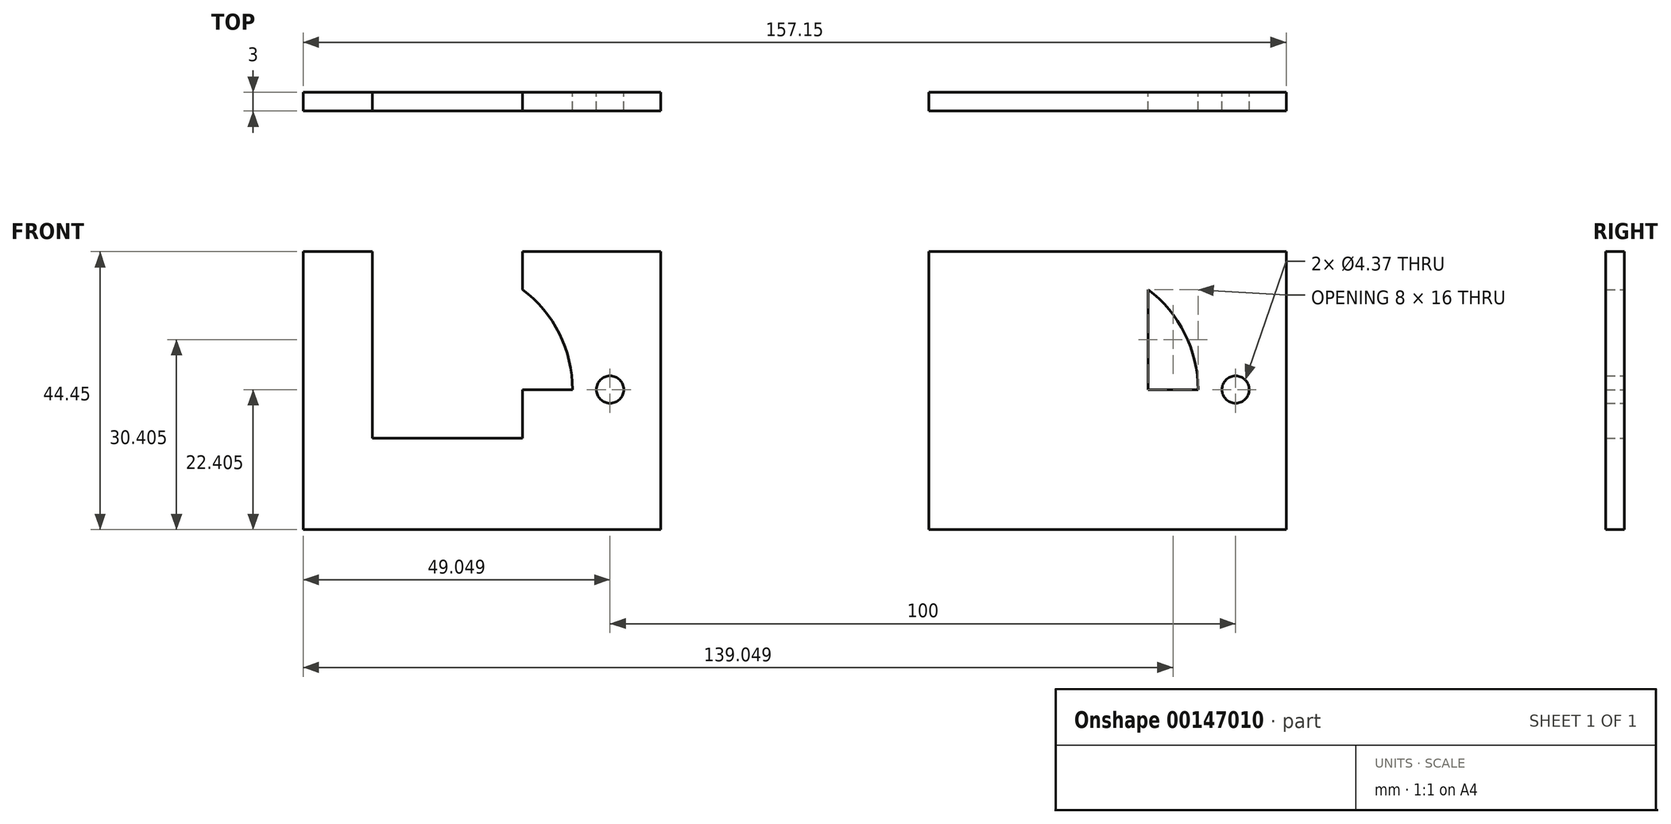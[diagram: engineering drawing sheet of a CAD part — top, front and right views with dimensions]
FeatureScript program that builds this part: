
annotation { "Feature Type Name" : "Feature", "Feature Type Description" : "" }
export const myFeature = defineFeature(function(context is Context, id is Id, definition is map)
    precondition{}
    {
        {
            var Q0;
            Q0=qCreatedBy(makeId("Front.planeOp"),FACE);
            var sketch = newSketch(context, id + "F0", { "sketchPlane" : qUnion([Q0])});
            skLineSegment(sketch, "E0.bottom", {"start": v(-38.32, 42.55) * mm, "end": v(34.07, 42.55) * mm});
            skLineSegment(sketch, "E0.top", {"start": v(-38.32, -29.84) * mm, "end": v(34.07, -29.84) * mm});
            skLineSegment(sketch, "E0.left", {"start": v(-38.32, 42.55) * mm, "end": v(-38.32, -29.84) * mm});
            skLineSegment(sketch, "E0.right", {"start": v(34.07, 42.55) * mm, "end": v(34.07, -29.84) * mm});
            skCircle(sketch, "E1", {"center": v(-10.8, -16.7) * mm, "radius": 2.18 * mm});
            skCircle(sketch, "E2", {"center": v(9.15, 5.72) * mm, "radius": 2.18 * mm});
            skCircle(sketch, "E3", {"center": v(9.15, 5.72) * mm, "radius": 20 * mm});
            skCircle(sketch, "E4", {"center": v(-10.8, -16.7) * mm, "radius": 10 * mm});
            skCircle(sketch, "E5", {"center": v(-13.28, 18.86) * mm, "radius": 20 * mm});
            skCircle(sketch, "E6", {"center": v(9.15, 5.72) * mm, "radius": 6 * mm});
            skCircle(sketch, "E7", {"center": v(-13.28, 18.86) * mm, "radius": 2.18 * mm});
            skLineSegment(sketch, "E8", {"start": v(-13.28, 18.86) * mm, "end": v(9.15, 5.72) * mm});
            skLineSegment(sketch, "E9", {"start": v(9.15, 5.72) * mm, "end": v(-10.8, -16.7) * mm});
            skLineSegment(sketch, "E10", {"start": v(-13.28, 18.86) * mm, "end": v(-13.28, 42.55) * mm});
            skLineSegment(sketch, "E11", {"start": v(-19.28, 42.55) * mm, "end": v(-19.28, 19.08) * mm});
            skLineSegment(sketch, "E12.MirrorCS", {"start": v(-7.28, 42.55) * mm, "end": v(-7.28, 19.08) * mm});
            skPoint(sketch, "E13.orphan", {"position": v(-7.28, 19.08) * mm});
            skLineSegment(sketch, "E14", {"start": v(-19.28, 19.08) * mm, "end": v(-19.28, 14.57) * mm});
            skLineSegment(sketch, "E15", {"start": v(-7.28, 19.08) * mm, "end": v(-7.28, 13.33) * mm});
            skLineSegment(sketch, "E16", {"start": v(-7.28, 13.33) * mm, "end": v(-19.28, 13.33) * mm});
            skLineSegment(sketch, "E17", {"start": v(-19.28, 13.33) * mm, "end": v(-19.28, 14.57) * mm});
            skLineSegment(sketch, "E18", {"start": v(-19.28, 42.55) * mm, "end": v(-19.28, 13.33) * mm});
            skLineSegment(sketch, "E19", {"start": v(-7.28, 42.55) * mm, "end": v(-7.28, 13.33) * mm});
            skLineSegment(sketch, "E20.bottom", {"start": v(-24.33, -118.82) * mm, "end": v(32.82, -118.82) * mm});
            skLineSegment(sketch, "E20.top", {"start": v(-24.33, -163.27) * mm, "end": v(32.82, -163.27) * mm});
            skLineSegment(sketch, "E20.left", {"start": v(-24.33, -118.82) * mm, "end": v(-24.33, -163.27) * mm});
            skLineSegment(sketch, "E20.right", {"start": v(32.82, -118.82) * mm, "end": v(32.82, -163.27) * mm});
            skCircle(sketch, "E21", {"center": v(24.72, -140.86) * mm, "radius": 2.18 * mm});
            skCircle(sketch, "E22", {"center": v(-1.28, -140.87) * mm, "radius": 20 * mm});
            skCircle(sketch, "E23", {"center": v(24.72, -140.86) * mm, "radius": 6 * mm});
            skCircle(sketch, "E24", {"center": v(-1.28, -140.87) * mm, "radius": 2.18 * mm});
            skLineSegment(sketch, "E25", {"start": v(-1.28, -140.87) * mm, "end": v(-1.28, -118.82) * mm});
            skLineSegment(sketch, "E26", {"start": v(-13.28, -118.82) * mm, "end": v(-13.28, -148.6) * mm});
            skLineSegment(sketch, "E27.MirrorCS", {"start": v(10.72, -118.82) * mm, "end": v(10.72, -148.6) * mm});
            skPoint(sketch, "E28.orphan", {"position": v(-1.28, -168.58) * mm});
            skLineSegment(sketch, "E29", {"start": v(10.72, -148.6) * mm, "end": v(-13.28, -148.6) * mm});
            skLineSegment(sketch, "E30", {"start": v(24.72, -140.86) * mm, "end": v(-1.28, -140.87) * mm});
            skSolve(sketch);
        }
        {
            var Q0;
            Q0=makeQuery(id+"F0.imprint","IMPRINT",FACE,{"disambiguationData":[TD([[makeQuery(id+"F0.imprint","IMPRINT",EDGE,{"derivedFrom":sQuery(id+"F0.wireOp",EDGE,"E20.top")}),1.0]])]});
            var Q1;
            {var subQ1=sQuery(id+"F0.wireOp",EDGE,"E29");Q1=makeQuery(id+"F0.imprint","IMPRINT",FACE,{"disambiguationData":[TD([[makeQuery(id+"F0.imprint","IMPRINT",EDGE,{"derivedFrom":subQ1}),1.0]])]});}
            var Q2;
            {var subQ0=sQuery(id+"F0.wireOp",EDGE,"E27.MirrorCS");var subQ1=sQuery(id+"F0.wireOp",EDGE,"E22");var subQ2=makeQuery(id+"F0.imprint","INTERSECT",VERTEX,{"derivedFrom":[subQ1,subQ0]});Q2=makeQuery(id+"F0.imprint","IMPRINT",FACE,{"disambiguationData":[TD([[makeQuery(id+"F0.imprint","IMPRINT",EDGE,{"disambiguationData":[TD([[subQ2,-1.0]])],"derivedFrom":subQ0}),1.0]])]});}
            var Q3;
            Q3=makeQuery(id+"F0.imprint","IMPRINT",FACE,{"disambiguationData":[TD([[makeQuery(id+"F0.imprint","IMPRINT",EDGE,{"derivedFrom":sQuery(id+"F0.wireOp",EDGE,"E21")}),-1.0]])]});
            extrude(context, id + "F1", {"entities" : qUnion([Q0, Q1, Q2, Q3]), "depth" : 3 * mm});
        }
        {
            var Q0;
            Q0=makeQuery(id+"F1.opExtrude","SWEPT_BODY",BODY,{"disambiguationData":[OSD([sQuery(id+"F0.wireOp",EDGE,"E20.bottom"),sQuery(id+"F0.wireOp",EDGE,"E20.top"),sQuery(id+"F0.wireOp",EDGE,"E20.left"),sQuery(id+"F0.wireOp",EDGE,"E20.right"),sQuery(id+"F0.wireOp",EDGE,"E21"),sQuery(id+"F0.wireOp",EDGE,"E29"),sQuery(id+"F0.wireOp",EDGE,"E26"),sQuery(id+"F0.wireOp",EDGE,"E27.MirrorCS")])]});
            transform(context, id + "F2", {"entities" : qUnion([Q0]), "transformType" : TransformType.TRANSLATION_3D, "dx" : 100 * mm, "dy" : 0 * mm, "dz" : 0 * mm, "makeCopy" : true});
        }
        {
            var Q0;
            Q0=makeQuery(id+"F2.opPattern","COPY",FACE,{"derivedFrom":makeQuery(id+"F1.opExtrude","CAP_FACE",FACE,{"disambiguationData":[OSD([sQuery(id+"F0.wireOp",EDGE,"E20.bottom"),sQuery(id+"F0.wireOp",EDGE,"E20.top"),sQuery(id+"F0.wireOp",EDGE,"E20.left"),sQuery(id+"F0.wireOp",EDGE,"E20.right"),sQuery(id+"F0.wireOp",EDGE,"E21"),sQuery(id+"F0.wireOp",EDGE,"E29"),sQuery(id+"F0.wireOp",EDGE,"E26"),sQuery(id+"F0.wireOp",EDGE,"E27.MirrorCS")])],"isStart":false}),"instanceName":"1"});
            var sketch = newSketch(context, id + "F3", { "sketchPlane" : qUnion([Q0])});
            skLineSegment(sketch, "E31.bottom", {"start": v(86.72, -118.82) * mm, "end": v(110.72, -118.82) * mm});
            skLineSegment(sketch, "E31.top", {"start": v(86.72, -148.6) * mm, "end": v(110.72, -148.6) * mm});
            skLineSegment(sketch, "E31.left", {"start": v(86.72, -118.82) * mm, "end": v(86.72, -148.6) * mm});
            skLineSegment(sketch, "E31.right", {"start": v(110.72, -118.82) * mm, "end": v(110.72, -148.6) * mm});
            skSolve(sketch);
        }
        {
            var Q0;
            Q0=makeQuery(id+"F3.imprint","IMPRINT",FACE,{"disambiguationData":[TD([[makeQuery(id+"F3.imprint","IMPRINT",EDGE,{"derivedFrom":sQuery(id+"F3.wireOp",EDGE,"E31.bottom")}),-1.0]])]});
            extrude(context, id + "F4", {"entities" : qUnion([Q0]), "operationType" : NewBodyOperationType.ADD, "oppositeDirection" : true, "depth" : 3 * mm});
        }
    });
